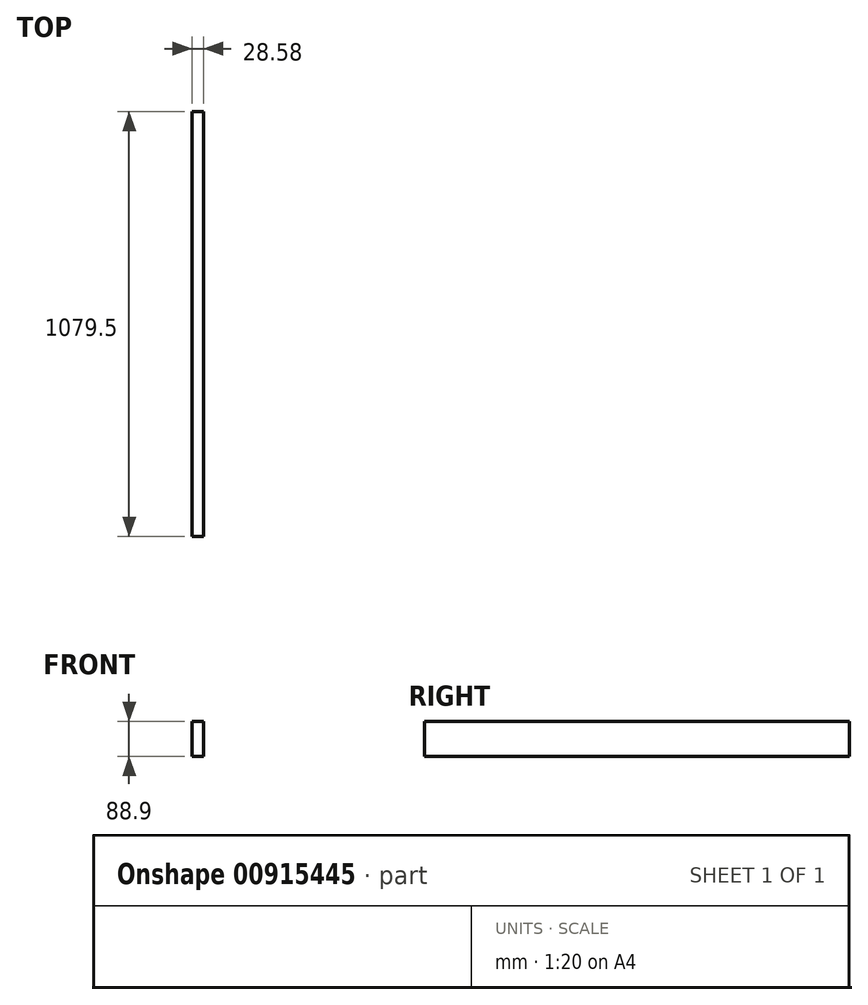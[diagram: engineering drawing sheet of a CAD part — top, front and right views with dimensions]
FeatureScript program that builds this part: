
annotation { "Feature Type Name" : "Feature", "Feature Type Description" : "" }
export const myFeature = defineFeature(function(context is Context, id is Id, definition is map)
    precondition{}
    {
        {
            var Q0;
            Q0=qCreatedBy(makeId("Front.planeOp"),FACE);
            var sketch = newSketch(context, id + "F0", { "sketchPlane" : qUnion([Q0])});
            skLineSegment(sketch, "E0.bottom", {"start": v(14.29, 44.45) * mm, "end": v(-14.29, 44.45) * mm});
            skLineSegment(sketch, "E0.top", {"start": v(14.29, -44.45) * mm, "end": v(-14.29, -44.45) * mm});
            skLineSegment(sketch, "E0.left", {"start": v(14.29, 44.45) * mm, "end": v(14.29, -44.45) * mm});
            skLineSegment(sketch, "E0.right", {"start": v(-14.29, 44.45) * mm, "end": v(-14.29, -44.45) * mm});
            skPoint(sketch, "E0.middle", {"position": v(0, 0) * mm});
            skSolve(sketch);
        }
        {
            var Q0;
            Q0=makeQuery(id+"F0.imprint","IMPRINT",FACE,{"disambiguationData":[TD([[makeQuery(id+"F0.imprint","IMPRINT",EDGE,{"derivedFrom":sQuery(id+"F0.wireOp",EDGE,"E0.bottom")}),1.0]])]});
            extrude(context, id + "F1", {"entities" : qUnion([Q0]), "oppositeDirection" : true, "depth" : 304.8 * mm, "offsetDistance" : 25.4 * mm, "hasSecondDirection" : true, "secondDirectionOppositeDirection" : false, "secondDirectionDepth" : 774.7 * mm});
        }
    });
